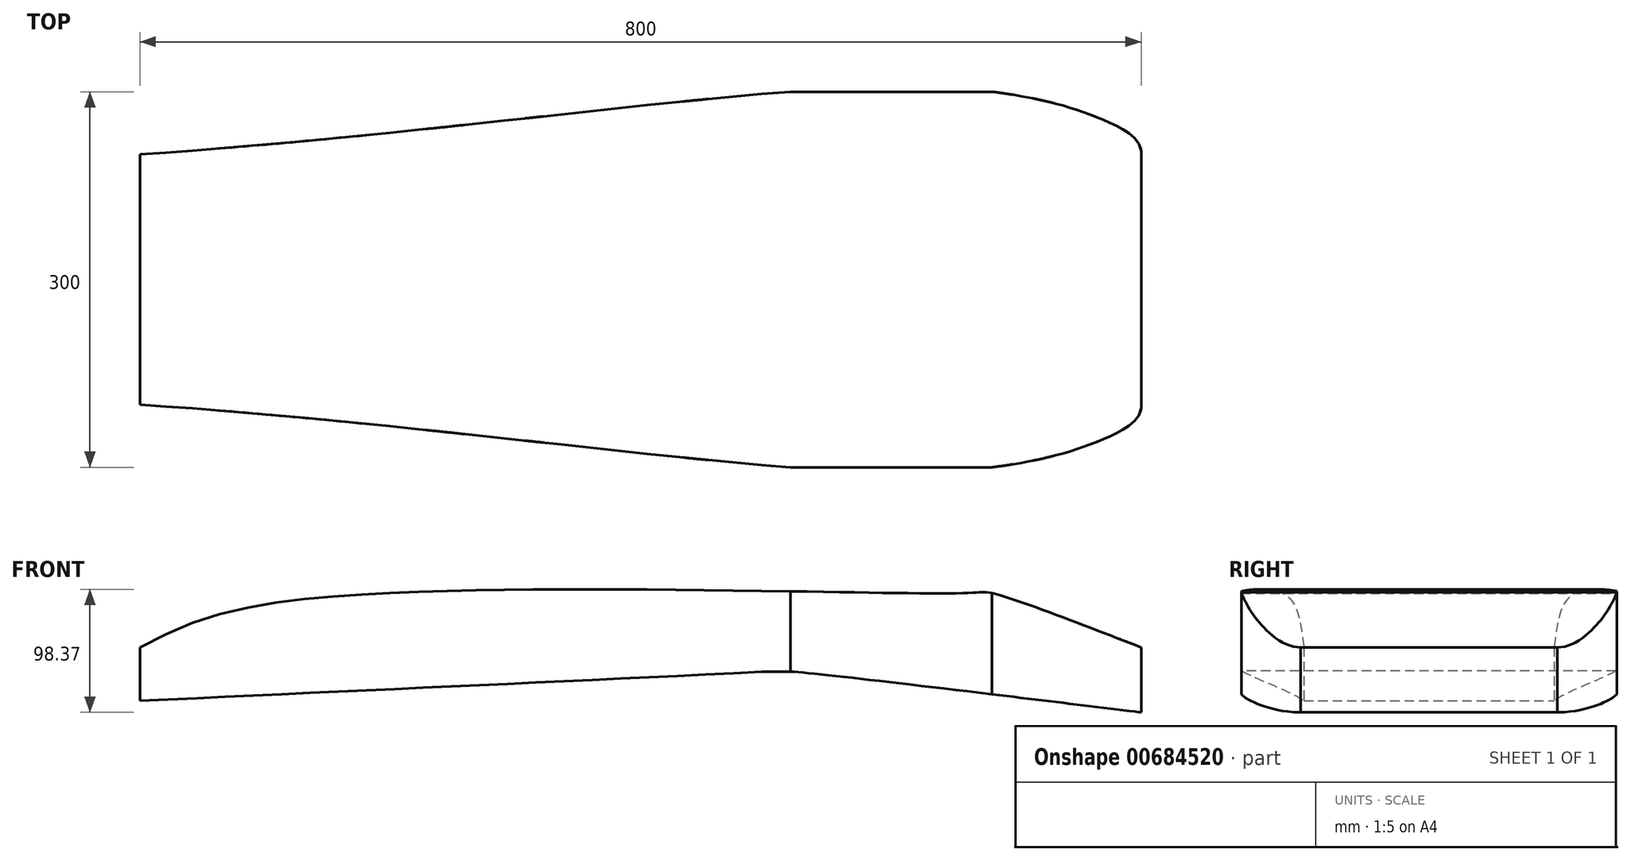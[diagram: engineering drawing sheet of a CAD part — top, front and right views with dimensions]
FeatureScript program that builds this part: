
annotation { "Feature Type Name" : "Feature", "Feature Type Description" : "" }
export const myFeature = defineFeature(function(context is Context, id is Id, definition is map)
    precondition{}
    {
        {
            var Q0;
            Q0=qCreatedBy(makeId("Top.planeOp"),FACE);
            var sketch = newSketch(context, id + "F0", { "sketchPlane" : qUnion([Q0])});
            skLineSegment(sketch, "E0.left", {"start": v(400, 100) * mm, "end": v(400, -100) * mm});
            skLineSegment(sketch, "E0.right", {"start": v(-400, 100) * mm, "end": v(-400, -100) * mm});
            skPoint(sketch, "E0.middle", {"position": v(0, 0) * mm});
            skLineSegment(sketch, "E1", {"start": v(-400, 0) * mm, "end": v(400, 0) * mm, "construction": true});
            skFitSpline(sketch, "E2", {"points": [v(-400, 100) * mm, v(185.93, 153.68) * mm, v(319.7, 143.38) * mm, v(370.56, 127.2) * mm, v(400, 100) * mm], "startDerivative": vector(1416.27, 94.19) * mm, "endDerivative": vector(-27.03, -305.58) * mm});
            skFitSpline(sketch, "E3.MirrorCS", {"points": [v(-400, -100) * mm, v(185.93, -153.68) * mm, v(319.7, -143.38) * mm, v(370.56, -127.2) * mm, v(400, -100) * mm], "startDerivative": vector(1416.27, -94.19) * mm, "endDerivative": vector(-27.03, 305.58) * mm});
            skSolve(sketch);
        }
        {
            var Q0;
            Q0=makeQuery(id+"F0.imprint","IMPRINT",FACE,{"disambiguationData":[TD([[makeQuery(id+"F0.imprint","IMPRINT",EDGE,{"derivedFrom":sQuery(id+"F0.wireOp",EDGE,"E0.left")}),-1.0]])]});
            extrude(context, id + "F1", {"entities" : qUnion([Q0]), "depth" : 150 * mm, "offsetDistance" : 25 * mm});
        }
        {
            var Q0;
            Q0=qCreatedBy(makeId("Front.planeOp"),FACE);
            var sketch = newSketch(context, id + "F2", { "sketchPlane" : qUnion([Q0])});
            skLineSegment(sketch, "E4.0.1", {"start": v(-400, 32.35) * mm, "end": v(-400, 75) * mm});
            skFitSpline(sketch, "E4.0.2", {"points": [v(-400, 150) * mm, v(-133.31, 150) * mm, v(133.37, 150) * mm, v(400.06, 150) * mm]});
            skLineSegment(sketch, "E4.0.3", {"start": v(400, 75) * mm, "end": v(400, 23.04) * mm});
            skFitSpline(sketch, "E5", {"points": [v(400, 75) * mm, v(280.2, 118.43) * mm, v(260.43, 118.43) * mm, v(-266.5, 113.77) * mm, v(-400, 75) * mm], "startDerivative": vector(-687.48, 266.21) * mm, "endDerivative": vector(-373.95, -198.18) * mm});
            skFitSpline(sketch, "E6", {"points": [v(400, 23.04) * mm, v(120.85, 55.61) * mm, v(98.75, 55.61) * mm, v(-400, 32.35) * mm], "startDerivative": vector(-962.36, 117.1) * mm, "endDerivative": vector(-1323.71, -60.75) * mm});
            skPoint(sketch, "E7.orphan", {"position": v(400, 150) * mm});
            skPoint(sketch, "E8.orphan", {"position": v(-400, 0) * mm});
            skPoint(sketch, "E9.orphan", {"position": v(400, 0) * mm});
            skPoint(sketch, "E10.orphan", {"position": v(-400, 150) * mm});
            skSolve(sketch);
        }
        {
            var Q0;
            Q0 = qSketchRegion(id + "F2", true);
            extrude(context, id + "F3", {"entities" : qUnion([Q0]), "operationType" : NewBodyOperationType.INTERSECT, "endBound" : BoundingType.SYMMETRIC, "depth" : 300 * mm, "offsetDistance" : 25 * mm});
        }
    });
